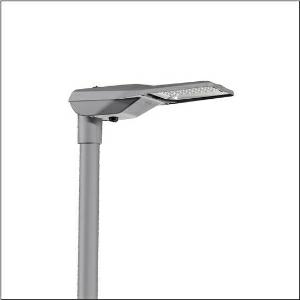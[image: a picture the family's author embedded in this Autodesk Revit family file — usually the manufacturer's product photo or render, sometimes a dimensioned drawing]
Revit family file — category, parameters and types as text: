
# Revit family: streetlight_sl_21_iq_mini___p0_5a_5xe2v31y08hb_0b7f
name_source: partatom
category: Lighting Fixtures
units: mm (PartAtom-declared; Revit-internal decimal feet)

## family parameters
Cut with Voids When Loaded = No
Host = Face
Light Source = No
Part Type = Normal
Room Calculation Point = No
Round Connector Dimension = Use Diameter
Shared = No

## types (1)
- --- (1 x LED, 9580 lm, 71 W, 3000K)
    Apparent Load = 71 VA
    CIE Flux Codes = 37 73 96 100 100
    Color Rendering = 70
    Color Temperature = 3000K
    Default Elevation = 1800 mm
    Description = Streetlight SL 21 iQ mini, mast luminaire, primary light control with lens, of PMMA, primary optical cover: cover, of toughened safety glass, transparent, light distribution: P0.5a, light emission: direct distribution, primary light characteristic: asymmetric, installation type: post-top, side-entry, LED, High Power LED, rated luminous flux: 9.580lm, luminous efficacy: 135lm/W, light colour: 730, colour temperature: 3000K, control gear: iQ-Street Remote, D4i with power reduction, control: pre-setting: logarithmic dimming characteristic, Street-Remote, Auto-Match, Temp-Guard, Lumen-Switch, Night-Set, Smart-Wire, Light-Fading, Desk-Remote (wireless, voltage-free reading and setting of iQ features in the workshop via application-optimized NFC function/RFID function), optimised constant luminous flux control (CLO 2.0), mains connection: 220..240V, AC, 50/60Hz, start of lifetime: 71W, end of service life: 75W, reduction: 30W, luminaire housing, of diecast aluminium, powder-coated, SITECO metallic grey (DB 702S), corrosivity category C5 high according to DIN EN ISO 12944, please order mast flange separately, inclination adjustable: 0°, 5°, 10°, 15°, sealing non-destructively replaceable, multi-level sealing system, length: 628mm, width: 235mm, height: 110mm, mast flange for spigot size: 42mm (side-entry): 5XC10008XM4, 60/48mm (side-entry/post-top): 5XC10108XM2, 76/60mm (side-entry/post-top): 5XC10108XM1, mounting height: 4..8m, Smart Interface below and above, protection rating (complete): IP66, insulation class (complete): insulation class II (safety insulation), certification: CE, ENEC, ENEC+, VDE, impact resistance: IK10, permissible operating ambient temperature for outdoor applications: -40..+50°C, standard-compliant lighting for roads and squares, packaging unit: 1 piece

Light Distribution: P0.5a
    Height = 110 mm
    Lamp = 1 x LED
    Lamp Light Flux = 9580 lm
    Lamp Power = 71 W
    Lamp count = 1
    Length = 625 mm
    Luminous efficacy = 135 lm/W
    Manufacturer = Siteco
    ModVariant = No
    Model = 5XE2V31Y08HB
    Number of Poles = 1
    OnlyDefault = Yes
    Power Factor = 1
    Product Name = Streetlight SL 21 iQ mini | P0.5a
    Product group = mast luminaire | pylon top
    ProductGroupID = 6100
    Protection Class = Protection class II
    Protection Degree = IP 66
    RLX_Detail_Level = 1
    RLX_Emergency_Light_Flux = 0 lm
    RLX_Emergency_Type = 0
    RLX_Emergency_Type_DB = No
    RlxData = <blob elided: 92209 chars, md5=f91d8652>
    Socket = socket
    Standby Power = 0 W
    System Light Flux = 9580 lm
    System Power = 71 W
    Type Comments = factory setting: luminous flux: 100 % | dim-lin: 254 | 716 mA
    Type Image = l_1003514.jpg
    URL = http://relux.com
    VarID = @adj_078297
    Voltage = 0 V
    Weight = 0.00 kg
    Width = 234 mm

## geometry (parser evidence)
native form markers: Blend x4, Sweep x11
no freeform markers — native parametric forms only
